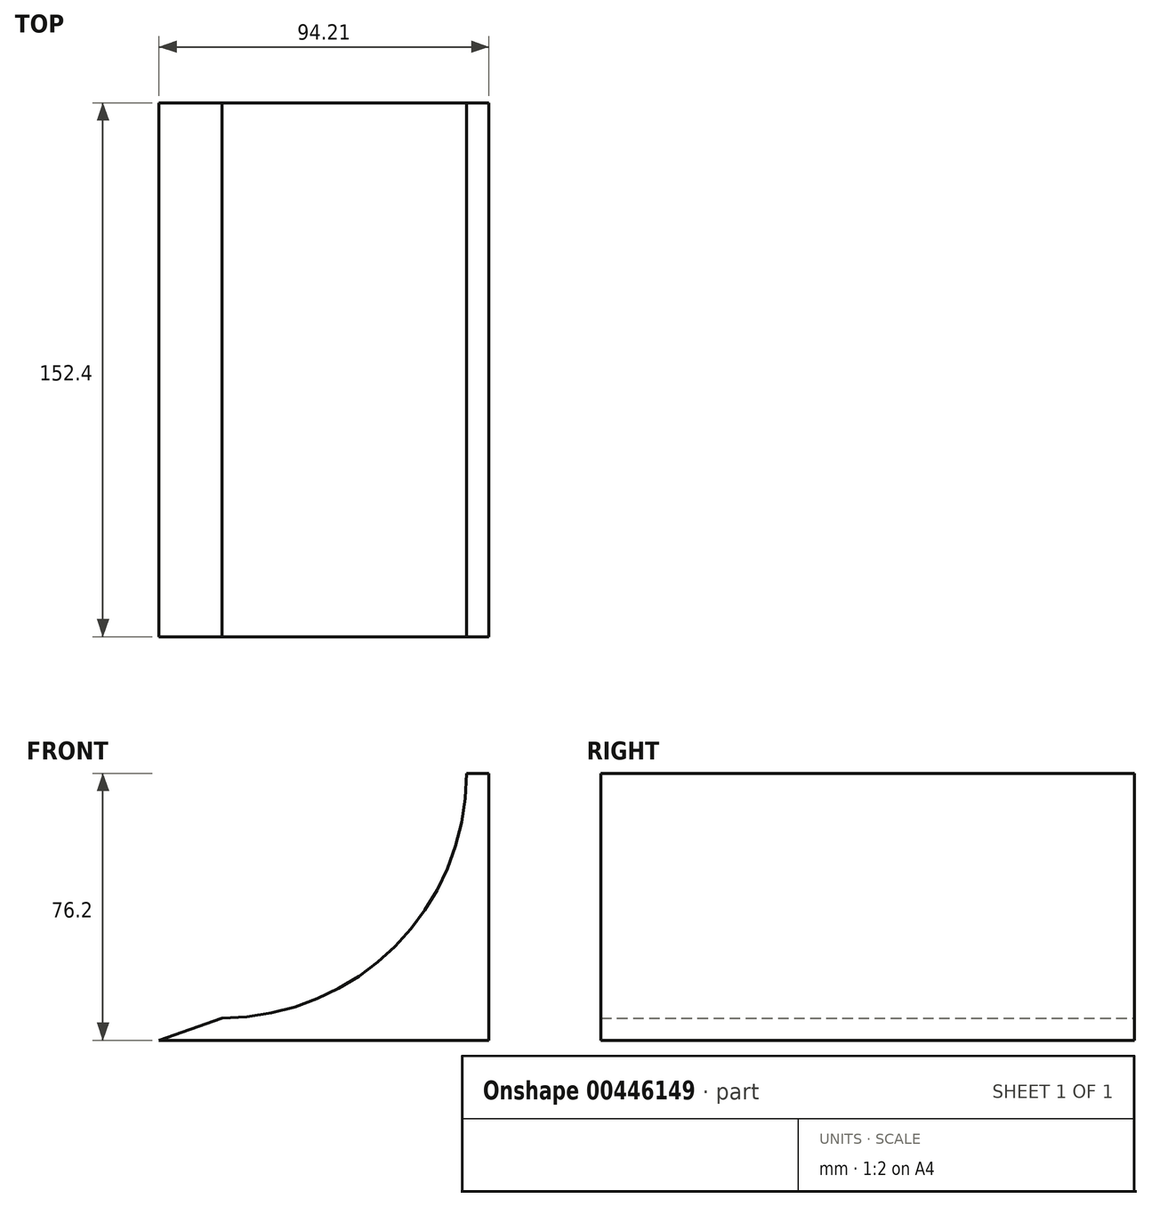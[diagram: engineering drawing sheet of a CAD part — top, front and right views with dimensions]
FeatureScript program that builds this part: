
annotation { "Feature Type Name" : "Feature", "Feature Type Description" : "" }
export const myFeature = defineFeature(function(context is Context, id is Id, definition is map)
    precondition{}
    {
        {
            var Q0;
            Q0=qCreatedBy(makeId("Front.planeOp"),FACE);
            var sketch = newSketch(context, id + "F0", { "sketchPlane" : qUnion([Q0])});
            skLineSegment(sketch, "E0.bottom", {"start": v(31.75, 35.72) * mm, "end": v(38.1, 35.72) * mm});
            skLineSegment(sketch, "E0.top", {"start": v(-38.1, -40.48) * mm, "end": v(38.1, -40.48) * mm});
            skLineSegment(sketch, "E0.right", {"start": v(38.1, 35.72) * mm, "end": v(38.1, -40.48) * mm});
            skArc(sketch, "E1", {"start": v(-38.1, -34.13) * mm, "mid": v(11.3, -13.67) * mm, "end": v(31.75, 35.72) * mm});
            skLineSegment(sketch, "E2", {"start": v(-38.1, -40.48) * mm, "end": v(-56.1, -40.48) * mm});
            skLineSegment(sketch, "E3", {"start": v(-56.1, -40.48) * mm, "end": v(-38.1, -34.13) * mm});
            skSolve(sketch);
        }
        {
            var Q0;
            Q0=makeQuery(id+"F0.imprint","IMPRINT",FACE,{"disambiguationData":[TD([[makeQuery(id+"F0.imprint","IMPRINT",EDGE,{"derivedFrom":sQuery(id+"F0.wireOp",EDGE,"E0.bottom")}),-1.0]])]});
            extrude(context, id + "F1", {"entities" : qUnion([Q0]), "depth" : 76.2 * mm});
        }
        {
            var Q0;
            Q0=makeQuery(id+"F1.opExtrude","CAP_FACE",FACE,{"disambiguationData":[OSD([sQuery(id+"F0.wireOp",EDGE,"E0.bottom"),sQuery(id+"F0.wireOp",EDGE,"E0.top"),sQuery(id+"F0.wireOp",EDGE,"E0.right"),sQuery(id+"F0.wireOp",EDGE,"E1"),sQuery(id+"F0.wireOp",EDGE,"E2"),sQuery(id+"F0.wireOp",EDGE,"E3")])],"isStart":false});
            extrude(context, id + "F2", {"entities" : qUnion([Q0]), "operationType" : NewBodyOperationType.ADD, "depth" : 76.2 * mm});
        }
    });
